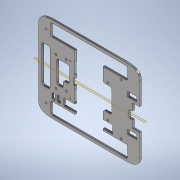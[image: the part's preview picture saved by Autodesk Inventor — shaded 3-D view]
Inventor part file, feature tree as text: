
AUTODESK INVENTOR PART (.ipt)
format: ipt  version: 2022 (Build 260153000, 153)  size: 848,896 bytes
history: native  units: mm
features: reference x67, other x54, sketch x16, projected_geometry x7, fillet x6
ambient origin geometry x8: Origin, YZ Plane, XZ Plane, XY Plane, X Axis, Y Axis, Z Axis, Center Point
bodies: Body1 (feature_tree)
feature tree (150):
  other  "Грань2"
  other  "Грань4"
  other  "Грань5"
  other  "Грань6"
  other  "Грань7"
  fillet  "Сопряжение1"  Radius=3.0mm
  fillet  "Сопряжение3"  Radius=4.0mm
  fillet  "Сопряжение4"  Radius=8.0mm
  other  "РабПлоскость1"
  fillet  "Сопряжение5"  Radius=4.0mm
  fillet  "Сопряжение6"  Radius=8.0mm
  fillet  "Сопряжение7"  Radius=4.0mm
  sketch  "Эскиз1"
  reference  "Ссылка1"
  reference  "Ссылка2"
  reference  "Ссылка9"
  other  "Пластина2"
  reference  "Ссылка12"
  reference  "Ссылка13"
  sketch  "Эскиз2"
  projected_geometry  "Спроецированная петля1"
  other  "Пластина4"
  other  "Сгиб2"
  reference  "Ссылка16"
  projected_geometry  "Спроецированная петля2"
  sketch  "Эскиз5"
  sketch  "Эскиз6"
  reference  "Ссылка21"
  reference  "Ссылка22"
  other  "Пластина5"
  other  "Сгиб3"
  projected_geometry  "Спроецированная петля3"
  reference  "Ссылка23"
  reference  "Ссылка24"
  other  "Пластина6"
  other  "Сгиб4"
  reference  "Ссылка25"
  sketch  "Эскиз8"
  reference  "Ссылка26"
  sketch  "Эскиз10"
  reference  "Ссылка27"
  reference  "Ссылка28"
  reference  "Ссылка29"
  other  "Пластина7"
  other  "Сгиб5"
  reference  "Ссылка30"
  reference  "Ссылка31"
  reference  "Ссылка32"
  reference  "Ссылка33"
  reference  "Ссылка34"
  reference  "Ссылка35"
  sketch  "Эскиз11"
  reference  "Ссылка36"
  reference  "Ссылка37"
  reference  "Ссылка38"
  reference  "Ссылка39"
  projected_geometry  "Спроецированная петля4"
  reference  "Ссылка42"
  reference  "Ссылка43"
  reference  "Ссылка44"
  reference  "Ссылка45"
  reference  "Ссылка46"
  reference  "Ссылка56"
  reference  "Ссылка57"
  reference  "Ссылка58"
  reference  "Ссылка59"
  sketch  "Эскиз18"
  reference  "Ссылка70"
  reference  "Ссылка71"
  reference  "Ссылка72"
  projected_geometry  "Спроецированная петля6"
  reference  "Ссылка73"
  reference  "Ссылка74"
  reference  "Ссылка75"
  reference  "Ссылка76"
  reference  "Ссылка77"
  reference  "Ссылка78"
  reference  "Ссылка79"
  reference  "Ссылка80"
  reference  "Ссылка81"
  reference  "Ссылка82"
  reference  "Ссылка83"
  reference  "Ссылка84"
  reference  "Ссылка85"
  reference  "Ссылка86"
  sketch  "Эскиз19"
  reference  "Ссылка87"
  reference  "Ссылка88"
  reference  "Ссылка89"
  reference  "Ссылка90"
  reference  "Ссылка91"
  sketch  "Эскиз20"
  projected_geometry  "Спроецированная петля7"
  sketch  "Эскиз21"
  reference  "Ссылка92"
  projected_geometry  "Спроецированная петля8"
  reference  "Ссылка93"
  sketch  "Эскиз22"
  reference  "Ссылка98"
  reference  "Ссылка99"
  sketch  "Эскиз23"
  reference  "Ссылка100"
  reference  "Ссылка101"
  sketch  "Эскиз24"
  reference  "Ссылка102"
  reference  "Ссылка107"
  sketch  "Эскиз27"
  reference  "Ссылка108"
  sketch  "Эскиз28"
  reference  "Ссылка109"
  reference  "Ссылка110"
  other  "Вырез1"
  other  "Вырез3"
  other  "Вырез4"
  other  "Вырез5"
  other  "Вырез6"
  other  "Вырез7"
  other  "Вырез8"
  other  "Вырез11"
  other  "Вырез12"
  other  "Вырез13"
  other  "Вырез14"
  other  "Вырез15"
  other  "Вырез16"
  other  "Вырез17"
  other  "Вырез19"
  other  "Вырез20"
  other  "<userpath>\Documents\Git\MZCAT_2024\MZCAT_2.iam"
  other  "MZCAT_2.iam"
  other  "plan:1"
  other  "CAT_wheel:1"
  other  "base plate:2"
  other  "base:1"
  other  "<userpath>\Documents\Git\MZCAT_2024\MZCAT_4.iam"
  other  "MZCAT_4.iam"
  other  "vydacha_slide:1"
  other  "base plate:1"
  other  "OCS-D008 B:1"
  other  "commutationCATboard:1"
  other  "magazine_fixator:1"
  other  "magazine:1"
  other  "motherboard_plate:1"
  other  "concevik_mirror:1"
  other  "concevik:1"
  other  "SMT10x2pin:1"
  other  "kommutation_board:1"
  other  "back_diffuser:1"
  other  "User Library-PLS-3:1"
  other  "back_led_board:1"
  other  "wifi module:1"
